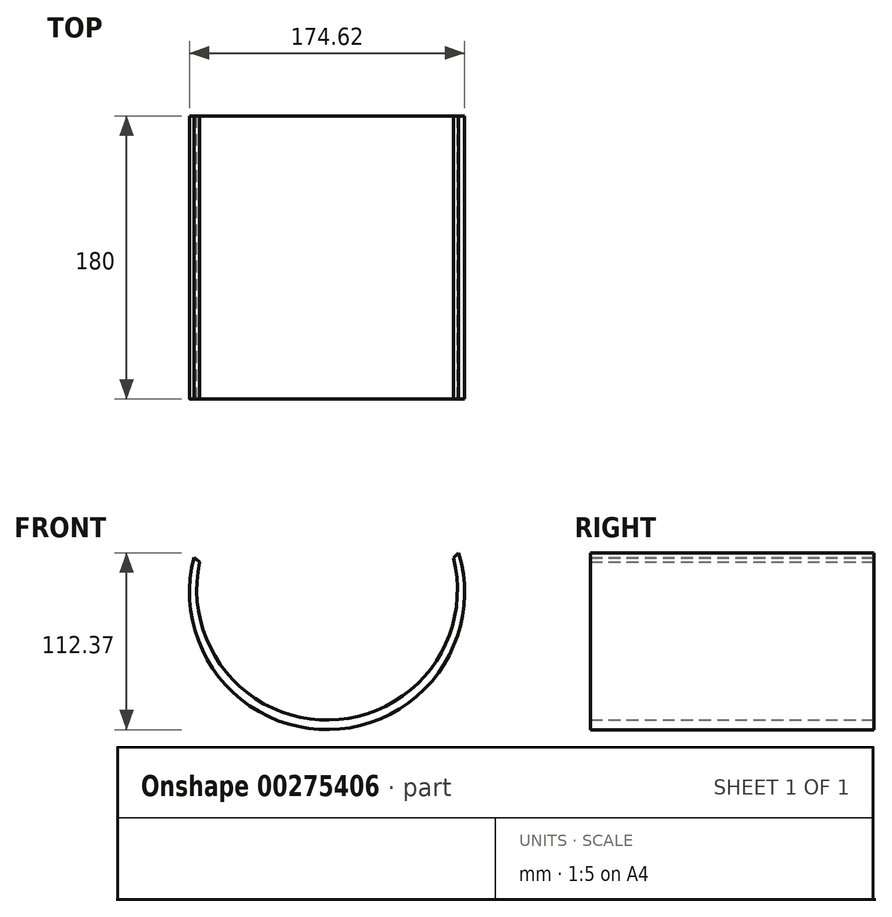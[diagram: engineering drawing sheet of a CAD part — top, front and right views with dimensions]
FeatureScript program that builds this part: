
annotation { "Feature Type Name" : "Feature", "Feature Type Description" : "" }
export const myFeature = defineFeature(function(context is Context, id is Id, definition is map)
    precondition{}
    {
        {
            var Q0;
            Q0=qCreatedBy(makeId("Front.planeOp"),FACE);
            var sketch = newSketch(context, id + "F0", { "sketchPlane" : qUnion([Q0])});
            skPoint(sketch, "E0.start.orphan", {"position": v(-163.04, 96.85) * mm});
            skArc(sketch, "E1", {"start": v(-109.51, 74.4) * mm, "mid": v(-32.28, -55.03) * mm, "end": v(42.71, 75.71) * mm});
            skArc(sketch, "E2", {"start": v(-106.76, 71.4) * mm, "mid": v(-32.27, -48.95) * mm, "end": v(40.05, 72.71) * mm});
            skLineSegment(sketch, "E3", {"start": v(-117.5, 54.4) * mm, "end": v(-113.9, 51.4) * mm});
            skLineSegment(sketch, "E4", {"start": v(47.25, 54.05) * mm, "end": v(50.6, 57.34) * mm});
            skLineSegment(sketch, "E5", {"start": v(-109.51, 74.4) * mm, "end": v(-106.76, 71.4) * mm});
            skLineSegment(sketch, "E6", {"start": v(40.05, 72.71) * mm, "end": v(42.71, 75.71) * mm});
            skSolve(sketch);
        }
        {
            var Q0;
            {var subQ0=sQuery(id+"F0.wireOp",EDGE,"E3");Q0=makeQuery(id+"F0.imprint","IMPRINT",FACE,{"disambiguationData":[TD([[makeQuery(id+"F0.imprint","IMPRINT",EDGE,{"derivedFrom":subQ0}),-1.0]])]});}
            extrude(context, id + "F1", {"entities" : qUnion([Q0]), "depth" : 180 * mm, "offsetDistance" : 25 * mm});
        }
    });
